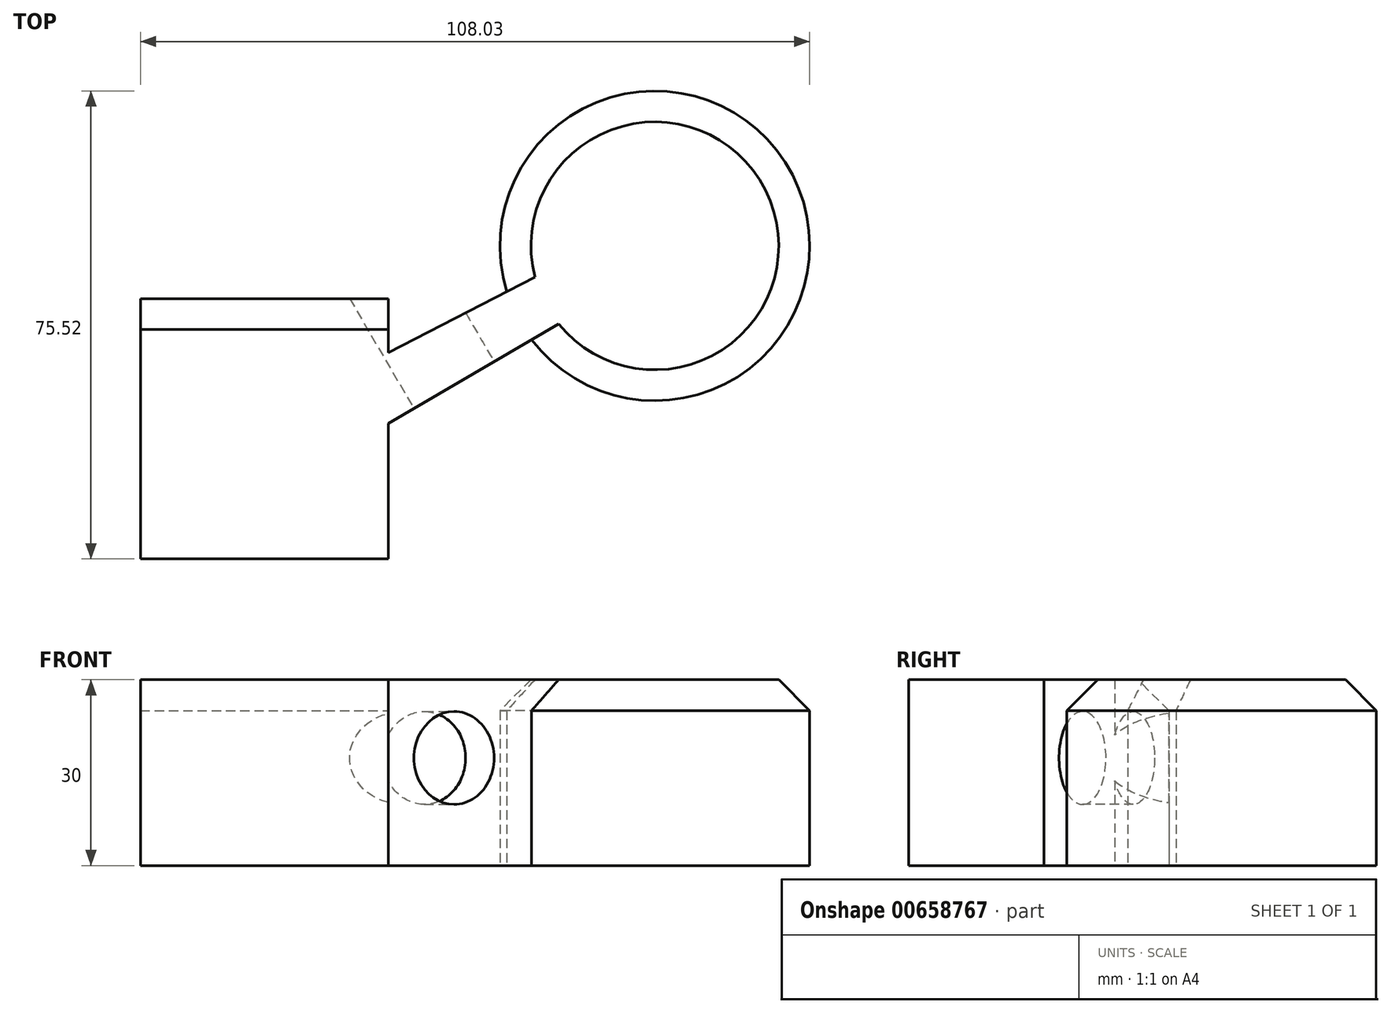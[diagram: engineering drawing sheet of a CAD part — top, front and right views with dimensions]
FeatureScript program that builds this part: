
annotation { "Feature Type Name" : "Feature", "Feature Type Description" : "" }
export const myFeature = defineFeature(function(context is Context, id is Id, definition is map)
    precondition{}
    {
        {
            var Q0;
            Q0=qCreatedBy(makeId("Top.planeOp"),FACE);
            var sketch = newSketch(context, id + "F0", { "sketchPlane" : qUnion([Q0])});
            skLineSegment(sketch, "E0.bottom", {"start": v(-46.93, 2.27) * mm, "end": v(-6.93, 2.27) * mm});
            skLineSegment(sketch, "E0.top", {"start": v(-46.93, -39.73) * mm, "end": v(-6.93, -39.73) * mm});
            skLineSegment(sketch, "E0.left", {"start": v(-46.93, 2.27) * mm, "end": v(-46.93, -39.73) * mm});
            skLineSegment(sketch, "E0.right", {"start": v(-6.93, 2.27) * mm, "end": v(-6.93, -6.47) * mm});
            skArc(sketch, "E1", {"start": v(16.2, -4.35) * mm, "mid": v(58.33, 22.22) * mm, "end": v(12.21, 3.41) * mm});
            skLineSegment(sketch, "E2", {"start": v(-6.93, -6.47) * mm, "end": v(12.21, 3.41) * mm});
            skLineSegment(sketch, "E3", {"start": v(-6.93, -17.89) * mm, "end": v(16.2, -4.35) * mm});
            skPoint(sketch, "E4.orphan", {"position": v(23.63, 0) * mm});
            skLineSegment(sketch, "E5.trimOffspring", {"start": v(-6.93, -17.89) * mm, "end": v(-6.93, -39.73) * mm});
            skSolve(sketch);
        }
        {
            var Q0;
            Q0 = qSketchRegion(id + "F0", true);
            extrude(context, id + "F1", {"entities" : qUnion([Q0]), "depth" : 30 * mm, "offsetDistance" : 25 * mm});
        }
        {
            var Q0;
            Q0=makeQuery(id+"F1.opExtrude","SWEPT_FACE",FACE,{"disambiguationData":[OSD([sQuery(id+"F0.wireOp",EDGE,"E3")])]});
            var sketch = newSketch(context, id + "F2", { "sketchPlane" : qUnion([Q0])});
            skCircle(sketch, "E6", {"center": v(-2.72, 17.37) * mm, "radius": 7.5 * mm});
            skSolve(sketch);
        }
        {
            var Q0;
            Q0=makeQuery(id+"F2.imprint","IMPRINT",FACE,{"disambiguationData":[TD([[makeQuery(id+"F2.imprint","IMPRINT",EDGE,{"derivedFrom":sQuery(id+"F2.wireOp",EDGE,"E6")}),1.0]])]});
            extrude(context, id + "F3", {"entities" : qUnion([Q0]), "operationType" : NewBodyOperationType.REMOVE, "endBound" : BoundingType.THROUGH_ALL, "oppositeDirection" : true, "depth" : 25 * mm, "offsetDistance" : 25 * mm});
        }
        {
            var Q0;
            Q0=makeQuery(id+"F1.opExtrude","CAP_EDGE",EDGE,{"disambiguationData":[OSD([sQuery(id+"F0.wireOp",EDGE,"E1")])],"isStart":false});
            var Q1;
            Q1=makeQuery(id+"F1.opExtrude","CAP_EDGE",EDGE,{"disambiguationData":[OSD([sQuery(id+"F0.wireOp",EDGE,"E0.bottom")])],"isStart":false});
            chamfer(context, id + "F4", {"entities" : qUnion([Q0, Q1]), "width" : 5 * mm, "tangentPropagation" : true});
        }
    });
